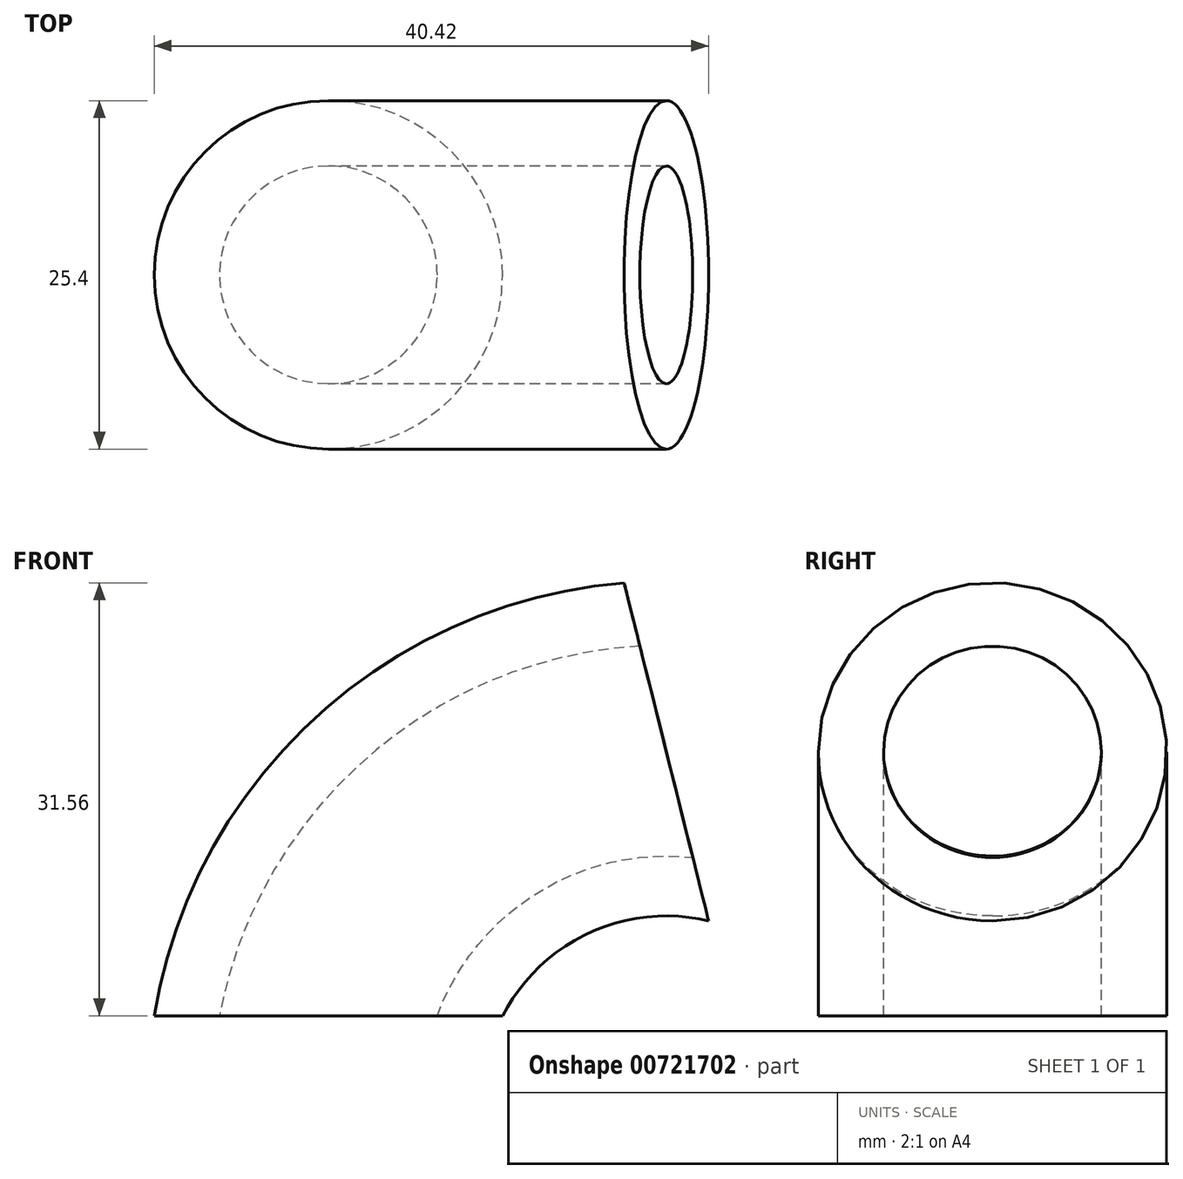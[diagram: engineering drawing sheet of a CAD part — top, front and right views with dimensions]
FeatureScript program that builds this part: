
annotation { "Feature Type Name" : "Feature", "Feature Type Description" : "" }
export const myFeature = defineFeature(function(context is Context, id is Id, definition is map)
    precondition{}
    {
        {
            var Q0;
            Q0=qCreatedBy(makeId("Front.planeOp"),FACE);
            var sketch = newSketch(context, id + "F0", { "sketchPlane" : qUnion([Q0])});
            skPoint(sketch, "E0.visualSharp", {"position": v(4518.56, 0) * mm});
            skPoint(sketch, "E1.orphan", {"position": v(-4518.56, 0) * mm});
            skPoint(sketch, "E2.visualSharp", {"position": v(-152.4, 0) * mm});
            skArc(sketch, "E3.filletArc", {"start": v(24.64, 19.24) * mm, "mid": v(9.01, 13.86) * mm, "end": v(0, 0) * mm});
            skSolve(sketch);
        }
        {
            var Q0;
            Q0=qCreatedBy(makeId("Top.planeOp"),FACE);
            var sketch = newSketch(context, id + "F1", { "sketchPlane" : qUnion([Q0])});
            skCircle(sketch, "E4", {"center": v(0, 0) * mm, "radius": 12.7 * mm});
            skCircle(sketch, "E5", {"center": v(0, 0) * mm, "radius": 7.94 * mm});
            skSolve(sketch);
        }
        {
            var Q0;
            Q0=qSketchRegion(id+"F1",true);
            var Q1;
            Q1=qConstructionFilter(qBodyType(qCreatedBy(id+"F0",EDGE),BodyType.WIRE),ConstructionObject.NO);
            sweep(context, id + "F2", {"profiles" : qUnion([Q0]), "path" : qUnion([Q1])});
        }
    });
